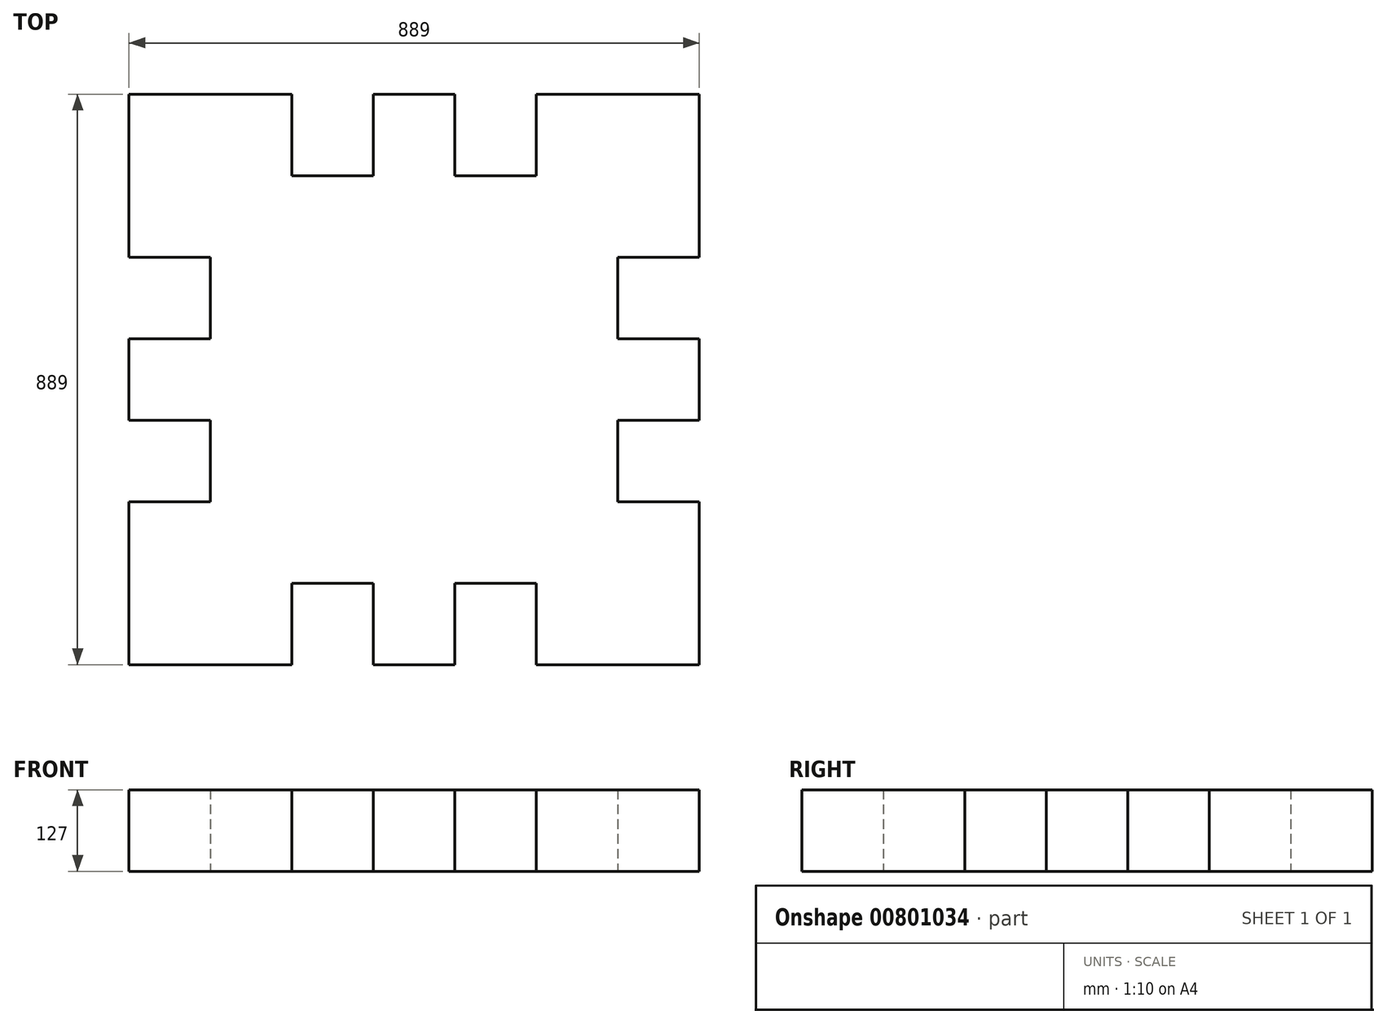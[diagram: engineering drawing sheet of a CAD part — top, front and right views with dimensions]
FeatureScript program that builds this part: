
annotation { "Feature Type Name" : "Feature", "Feature Type Description" : "" }
export const myFeature = defineFeature(function(context is Context, id is Id, definition is map)
    precondition{}
    {
        {
            var Q0;
            Q0=qCreatedBy(makeId("Top.planeOp"),FACE);
            var sketch = newSketch(context, id + "F0", { "sketchPlane" : qUnion([Q0])});
            skLineSegment(sketch, "E0.bottom", {"start": v(0, 0) * mm, "end": v(635, 0) * mm});
            skLineSegment(sketch, "E0.top", {"start": v(0, -635) * mm, "end": v(635, -635) * mm});
            skLineSegment(sketch, "E0.left", {"start": v(0, 0) * mm, "end": v(0, -635) * mm});
            skLineSegment(sketch, "E0.right", {"start": v(635, 0) * mm, "end": v(635, -635) * mm});
            skLineSegment(sketch, "E1.bottom", {"start": v(0, 0) * mm, "end": v(127, 0) * mm});
            skLineSegment(sketch, "E1.top", {"start": v(0, 127) * mm, "end": v(127, 127) * mm});
            skLineSegment(sketch, "E1.left", {"start": v(0, 0) * mm, "end": v(0, 127) * mm});
            skLineSegment(sketch, "E1.right", {"start": v(127, 0) * mm, "end": v(127, 127) * mm});
            skLineSegment(sketch, "E2.bottom", {"start": v(254, 0) * mm, "end": v(381, 0) * mm});
            skLineSegment(sketch, "E2.top", {"start": v(254, 127) * mm, "end": v(381, 127) * mm});
            skLineSegment(sketch, "E2.left", {"start": v(254, 0) * mm, "end": v(254, 127) * mm});
            skLineSegment(sketch, "E2.right", {"start": v(381, 0) * mm, "end": v(381, 127) * mm});
            skLineSegment(sketch, "E3.bottom", {"start": v(635, 0) * mm, "end": v(508, 0) * mm});
            skLineSegment(sketch, "E3.top", {"start": v(635, 127) * mm, "end": v(508, 127) * mm});
            skLineSegment(sketch, "E3.left", {"start": v(635, 0) * mm, "end": v(635, 127) * mm});
            skLineSegment(sketch, "E3.right", {"start": v(508, 0) * mm, "end": v(508, 127) * mm});
            skLineSegment(sketch, "E4.bottom", {"start": v(0, 0) * mm, "end": v(-127, 0) * mm});
            skLineSegment(sketch, "E4.top", {"start": v(0, -127) * mm, "end": v(-127, -127) * mm});
            skLineSegment(sketch, "E4.left", {"start": v(0, 0) * mm, "end": v(0, -127) * mm});
            skLineSegment(sketch, "E4.right", {"start": v(-127, 0) * mm, "end": v(-127, -127) * mm});
            skLineSegment(sketch, "E5.bottom", {"start": v(0, -254) * mm, "end": v(-127, -254) * mm});
            skLineSegment(sketch, "E5.top", {"start": v(0, -381) * mm, "end": v(-127, -381) * mm});
            skLineSegment(sketch, "E5.left", {"start": v(0, -254) * mm, "end": v(0, -381) * mm});
            skLineSegment(sketch, "E5.right", {"start": v(-127, -254) * mm, "end": v(-127, -381) * mm});
            skLineSegment(sketch, "E6.bottom", {"start": v(0, -635) * mm, "end": v(-127, -635) * mm});
            skLineSegment(sketch, "E6.top", {"start": v(0, -508) * mm, "end": v(-127, -508) * mm});
            skLineSegment(sketch, "E6.left", {"start": v(0, -635) * mm, "end": v(0, -508) * mm});
            skLineSegment(sketch, "E6.right", {"start": v(-127, -635) * mm, "end": v(-127, -508) * mm});
            skLineSegment(sketch, "E7.bottom", {"start": v(0, -635) * mm, "end": v(127, -635) * mm});
            skLineSegment(sketch, "E7.top", {"start": v(0, -762) * mm, "end": v(127, -762) * mm});
            skLineSegment(sketch, "E7.left", {"start": v(0, -635) * mm, "end": v(0, -762) * mm});
            skLineSegment(sketch, "E7.right", {"start": v(127, -635) * mm, "end": v(127, -762) * mm});
            skLineSegment(sketch, "E8.bottom", {"start": v(254, -635) * mm, "end": v(381, -635) * mm});
            skLineSegment(sketch, "E8.top", {"start": v(254, -762) * mm, "end": v(381, -762) * mm});
            skLineSegment(sketch, "E8.left", {"start": v(254, -635) * mm, "end": v(254, -762) * mm});
            skLineSegment(sketch, "E8.right", {"start": v(381, -635) * mm, "end": v(381, -762) * mm});
            skLineSegment(sketch, "E9.bottom", {"start": v(635, -635) * mm, "end": v(508, -635) * mm});
            skLineSegment(sketch, "E9.top", {"start": v(635, -762) * mm, "end": v(508, -762) * mm});
            skLineSegment(sketch, "E9.left", {"start": v(635, -635) * mm, "end": v(635, -762) * mm});
            skLineSegment(sketch, "E9.right", {"start": v(508, -635) * mm, "end": v(508, -762) * mm});
            skLineSegment(sketch, "E10.bottom", {"start": v(635, 0) * mm, "end": v(762, 0) * mm});
            skLineSegment(sketch, "E10.top", {"start": v(635, -127) * mm, "end": v(762, -127) * mm});
            skLineSegment(sketch, "E10.left", {"start": v(635, 0) * mm, "end": v(635, -127) * mm});
            skLineSegment(sketch, "E10.right", {"start": v(762, 0) * mm, "end": v(762, -127) * mm});
            skLineSegment(sketch, "E11.bottom", {"start": v(635, -508) * mm, "end": v(762, -508) * mm});
            skLineSegment(sketch, "E11.top", {"start": v(635, -635) * mm, "end": v(762, -635) * mm});
            skLineSegment(sketch, "E11.left", {"start": v(635, -508) * mm, "end": v(635, -635) * mm});
            skLineSegment(sketch, "E11.right", {"start": v(762, -508) * mm, "end": v(762, -635) * mm});
            skLineSegment(sketch, "E12.bottom", {"start": v(635, -254) * mm, "end": v(762, -254) * mm});
            skLineSegment(sketch, "E12.top", {"start": v(635, -381) * mm, "end": v(762, -381) * mm});
            skLineSegment(sketch, "E12.left", {"start": v(635, -254) * mm, "end": v(635, -381) * mm});
            skLineSegment(sketch, "E12.right", {"start": v(762, -254) * mm, "end": v(762, -381) * mm});
            skLineSegment(sketch, "E13.bottom", {"start": v(-127, 0) * mm, "end": v(0, 0) * mm});
            skLineSegment(sketch, "E13.top", {"start": v(-127, 127) * mm, "end": v(0, 127) * mm});
            skLineSegment(sketch, "E13.left", {"start": v(-127, 0) * mm, "end": v(-127, 127) * mm});
            skLineSegment(sketch, "E14.bottom", {"start": v(635, 127) * mm, "end": v(762, 127) * mm});
            skLineSegment(sketch, "E14.left", {"start": v(635, 127) * mm, "end": v(635, 0) * mm});
            skLineSegment(sketch, "E14.right", {"start": v(762, 127) * mm, "end": v(762, 0) * mm});
            skLineSegment(sketch, "E15.bottom", {"start": v(-127, -635) * mm, "end": v(0, -635) * mm});
            skLineSegment(sketch, "E15.top", {"start": v(-127, -762) * mm, "end": v(0, -762) * mm});
            skLineSegment(sketch, "E15.left", {"start": v(-127, -635) * mm, "end": v(-127, -762) * mm});
            skLineSegment(sketch, "E16.bottom", {"start": v(762, -635) * mm, "end": v(635, -635) * mm});
            skLineSegment(sketch, "E16.top", {"start": v(762, -762) * mm, "end": v(635, -762) * mm});
            skLineSegment(sketch, "E16.left", {"start": v(762, -635) * mm, "end": v(762, -762) * mm});
            skSolve(sketch);
        }
        {
            var Q0;
            Q0 = qSketchRegion(id + "F0", true);
            extrude(context, id + "F1", {"entities" : qUnion([Q0]), "depth" : 127 * mm, "offsetDistance" : 25.4 * mm});
        }
    });
